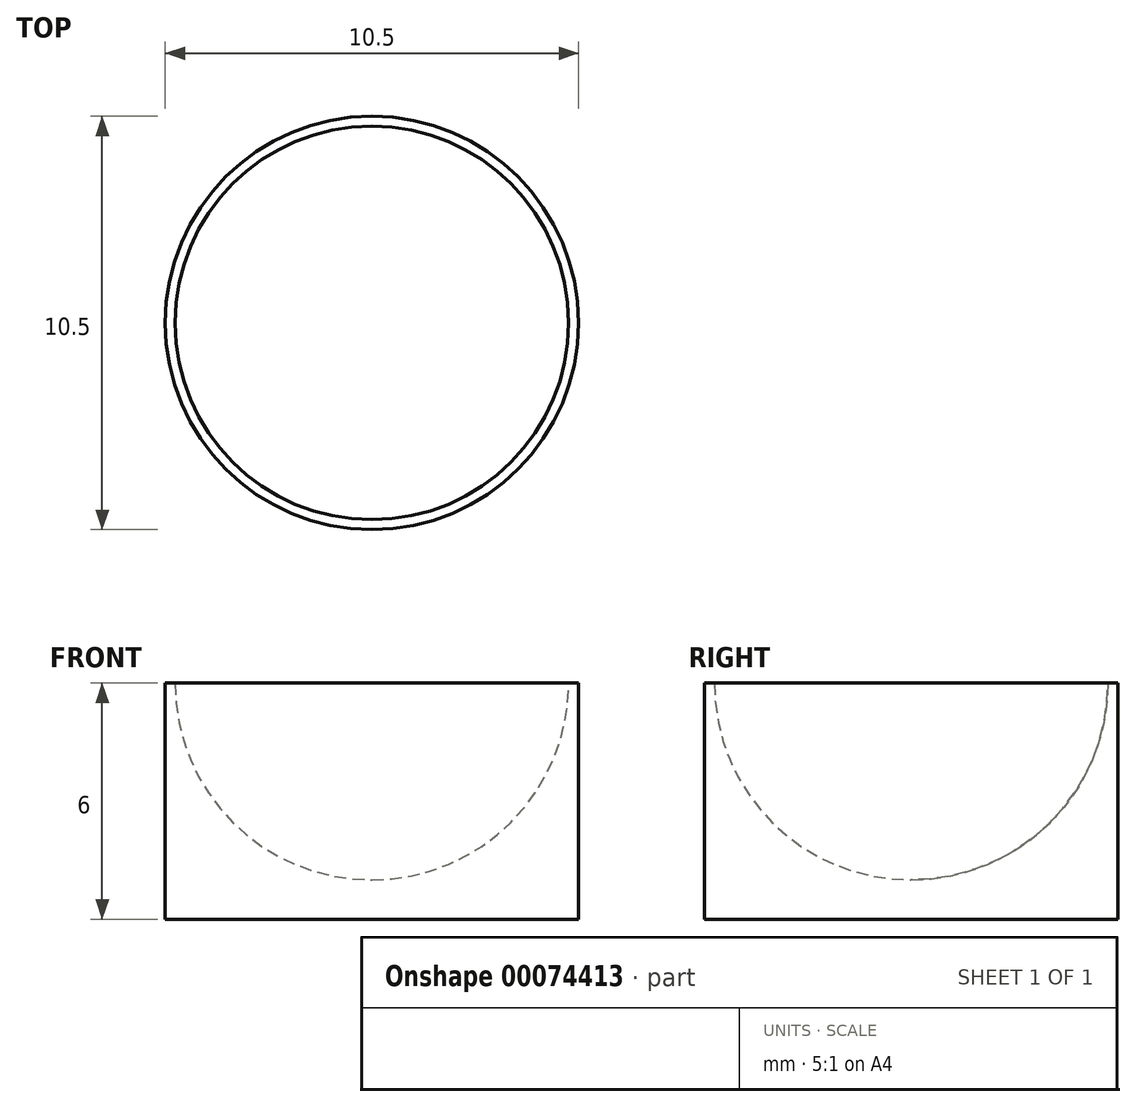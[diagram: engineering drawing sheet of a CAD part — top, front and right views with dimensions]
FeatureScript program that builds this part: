
annotation { "Feature Type Name" : "Feature", "Feature Type Description" : "" }
export const myFeature = defineFeature(function(context is Context, id is Id, definition is map)
    precondition{}
    {
        {
            var Q0;
            Q0=qCreatedBy(makeId("Right.planeOp"),FACE);
            var sketch = newSketch(context, id + "F0", { "sketchPlane" : qUnion([Q0])});
            skLineSegment(sketch, "E0", {"start": v(0, 0) * mm, "end": v(5.25, 0) * mm});
            skLineSegment(sketch, "E1", {"start": v(5.25, 0) * mm, "end": v(5.25, 6) * mm});
            skLineSegment(sketch, "E2", {"start": v(5.25, 6) * mm, "end": v(5, 6) * mm});
            skLineSegment(sketch, "E3", {"start": v(0, 0) * mm, "end": v(0, 1) * mm});
            skArc(sketch, "E4", {"start": v(0, 1) * mm, "mid": v(3.54, 2.46) * mm, "end": v(5, 6) * mm});
            skSolve(sketch);
        }
        {
            var Q0;
            Q0=makeQuery(id+"F0.imprint","IMPRINT",FACE,{"disambiguationData":[TD([[makeQuery(id+"F0.imprint","IMPRINT",EDGE,{"derivedFrom":sQuery(id+"F0.wireOp",EDGE,"E0")}),1.0]])]});
            var Q1;
            Q1=sQuery(id+"F0.wireOp",EDGE,"E3");
            revolve(context, id + "F1", {"entities" : qUnion([Q0]), "axis" : qUnion([Q1]), "revolveType" : RevolveType.FULL});
        }
    });
